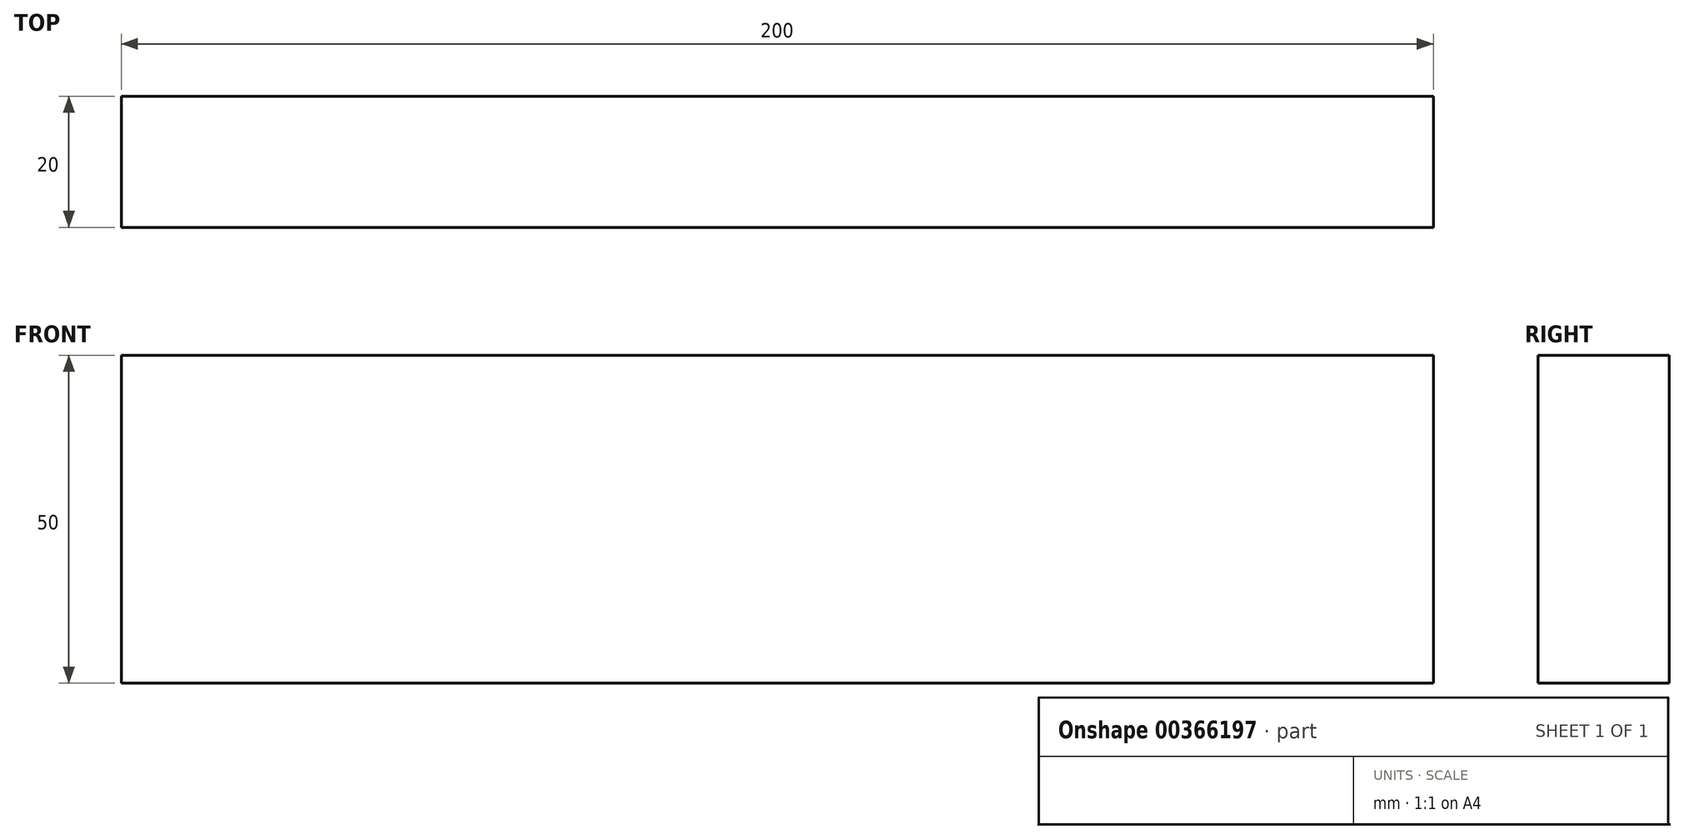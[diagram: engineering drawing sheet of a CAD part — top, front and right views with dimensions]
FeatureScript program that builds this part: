
annotation { "Feature Type Name" : "Feature", "Feature Type Description" : "" }
export const myFeature = defineFeature(function(context is Context, id is Id, definition is map)
    precondition{}
    {
        {
            var Q0;
            Q0=qCreatedBy(makeId("Top.planeOp"),FACE);
            var sketch = newSketch(context, id + "F0", { "sketchPlane" : qUnion([Q0])});
            skLineSegment(sketch, "E0.bottom", {"start": v(-100, -10) * mm, "end": v(100, -10) * mm});
            skLineSegment(sketch, "E0.top", {"start": v(-100, 10) * mm, "end": v(100, 10) * mm});
            skLineSegment(sketch, "E0.left", {"start": v(-100, -10) * mm, "end": v(-100, 10) * mm});
            skLineSegment(sketch, "E0.right", {"start": v(100, -10) * mm, "end": v(100, 10) * mm});
            skSolve(sketch);
        }
        {
            var Q0;
            Q0 = qSketchRegion(id + "F0", true);
            extrude(context, id + "F1", {"entities" : qUnion([Q0]), "endBound" : BoundingType.SYMMETRIC, "depth" : 50 * mm, "hasSecondDirection" : true, "secondDirectionOppositeDirection" : true, "secondDirectionDepth" : 25 * mm});
        }
    });
